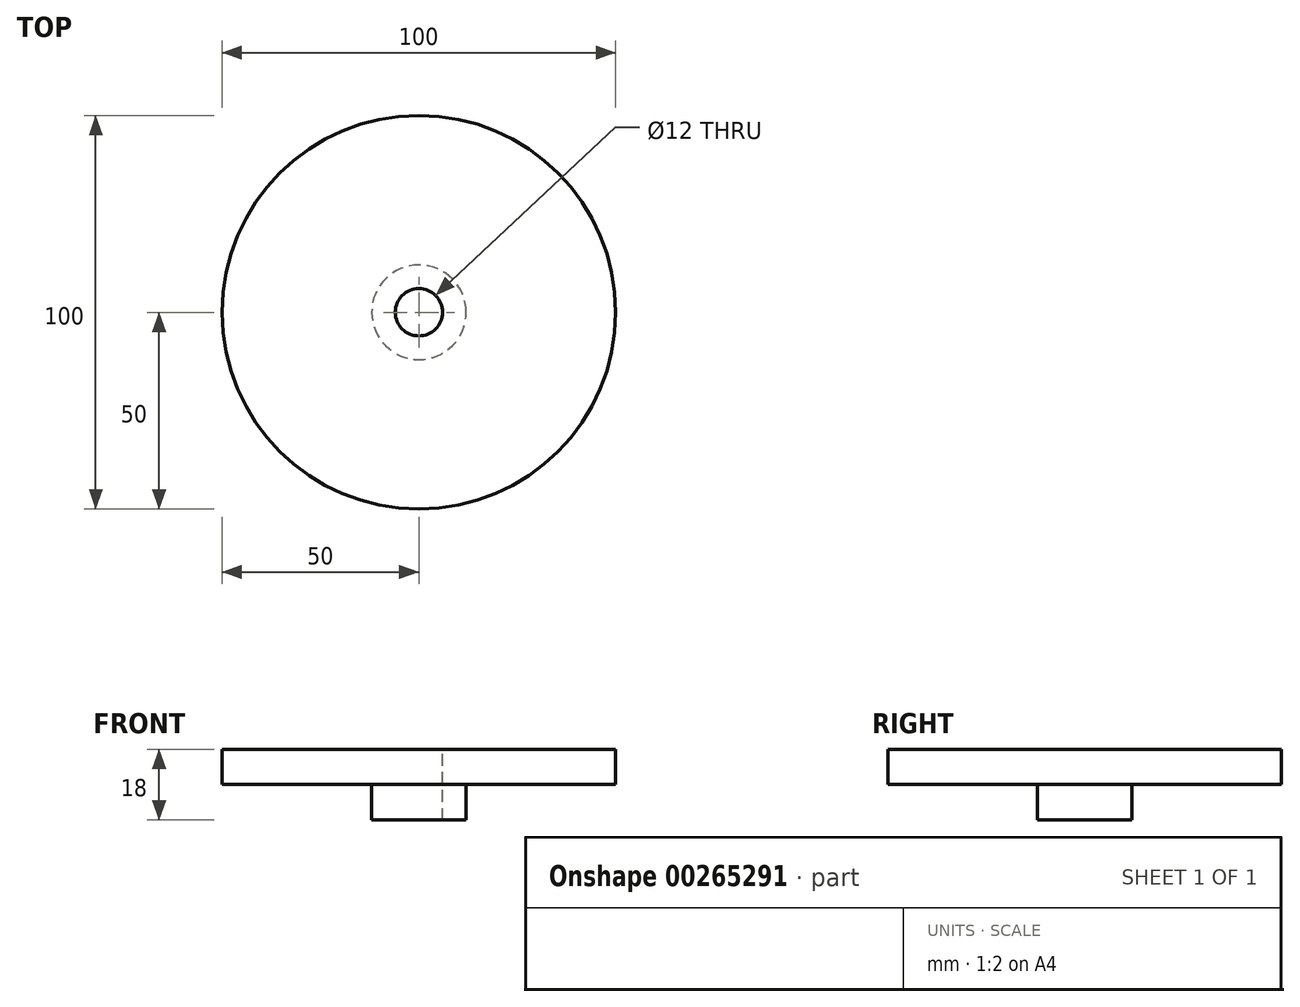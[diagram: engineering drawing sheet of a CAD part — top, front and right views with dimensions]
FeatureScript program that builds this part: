
annotation { "Feature Type Name" : "Feature", "Feature Type Description" : "" }
export const myFeature = defineFeature(function(context is Context, id is Id, definition is map)
    precondition{}
    {
        {
            var Q0;
            Q0=qCreatedBy(makeId("Right.planeOp"),FACE);
            var sketch = newSketch(context, id + "F0", { "sketchPlane" : qUnion([Q0])});
            skLineSegment(sketch, "E0", {"start": v(0, 0) * mm, "end": v(-6, 0) * mm, "construction": true});
            skLineSegment(sketch, "E1", {"start": v(-6, 0) * mm, "end": v(-50, 0) * mm});
            skLineSegment(sketch, "E2", {"start": v(-50, 0) * mm, "end": v(-50, -9) * mm});
            skLineSegment(sketch, "E3", {"start": v(-50, -9) * mm, "end": v(-12, -9) * mm});
            skLineSegment(sketch, "E4", {"start": v(-12, -9) * mm, "end": v(-12, -18) * mm});
            skLineSegment(sketch, "E5", {"start": v(-12, -18) * mm, "end": v(-6, -18) * mm});
            skLineSegment(sketch, "E6", {"start": v(-6, -18) * mm, "end": v(-6, 0) * mm});
            skLineSegment(sketch, "E7", {"start": v(0, 0) * mm, "end": v(0, -18.21) * mm, "construction": true});
            skSolve(sketch);
        }
        {
            var Q0;
            Q0=makeQuery(id+"F0.imprint","IMPRINT",FACE,{"disambiguationData":[TD([[makeQuery(id+"F0.imprint","IMPRINT",EDGE,{"derivedFrom":sQuery(id+"F0.wireOp",EDGE,"E1")}),1.0]])]});
            var Q1;
            Q1=sQuery(id+"F0.wireOp",EDGE,"E7");
            revolve(context, id + "F1", {"entities" : qUnion([Q0]), "axis" : qUnion([Q1]), "revolveType" : RevolveType.FULL});
        }
    });
